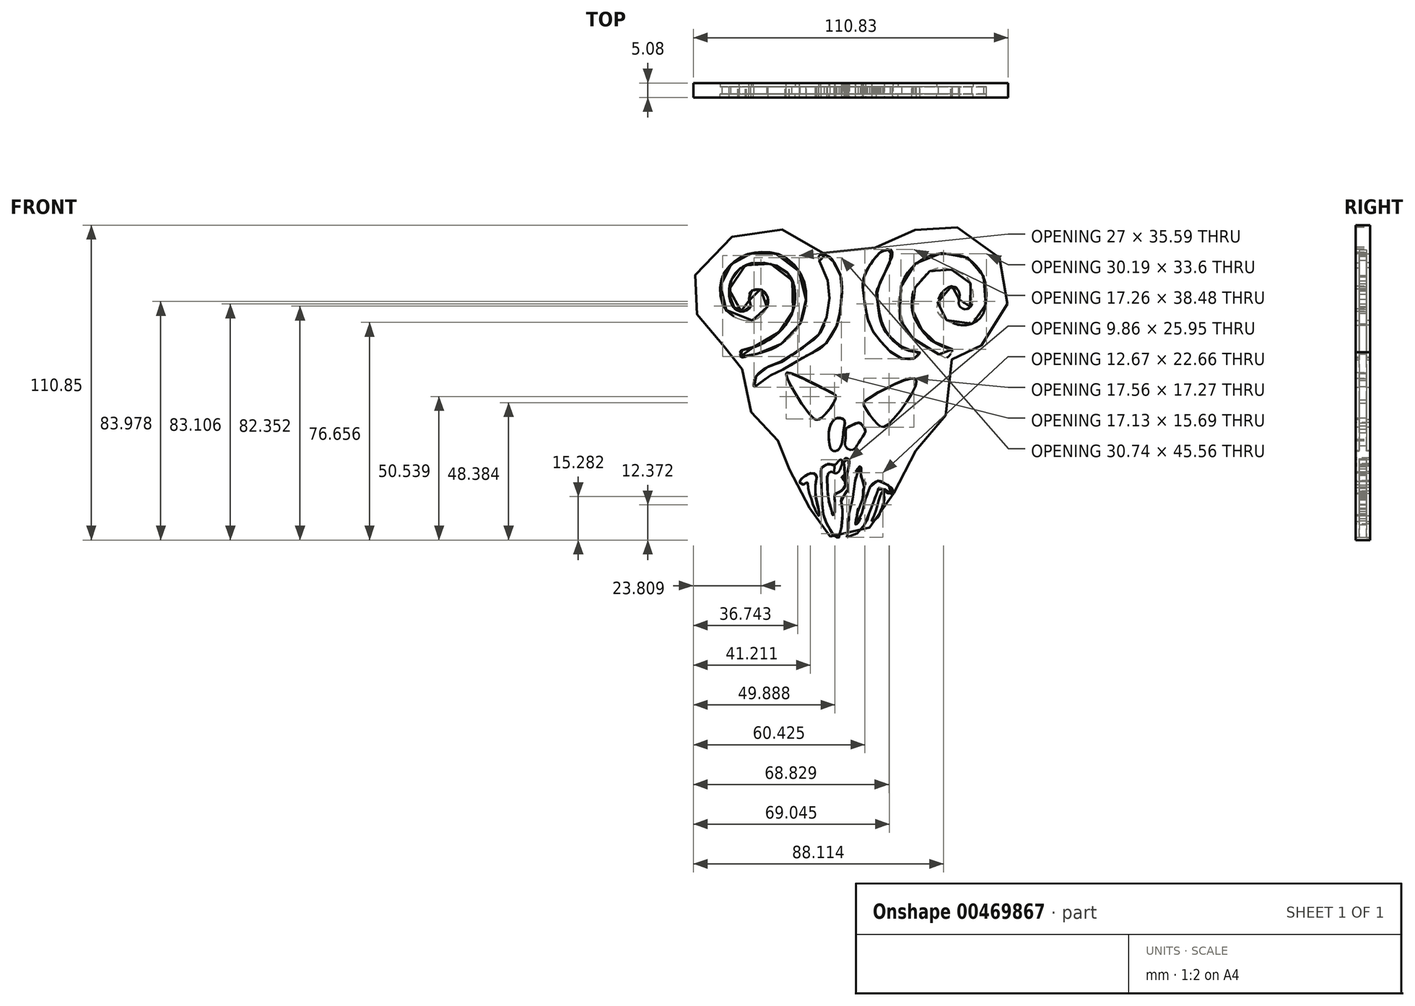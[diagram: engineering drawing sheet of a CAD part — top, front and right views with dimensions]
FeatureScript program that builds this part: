
annotation { "Feature Type Name" : "Feature", "Feature Type Description" : "" }
export const myFeature = defineFeature(function(context is Context, id is Id, definition is map)
    precondition{}
    {
        {
            var Q0;
            Q0=qCreatedBy(makeId("Front.planeOp"),FACE);
            var sketch = newSketch(context, id + "F0", { "sketchPlane" : qUnion([Q0])});
            skFitSpline(sketch, "E0", {"points": [v(-12.41, -53.78) * mm, v(-13.63, -52.56) * mm, v(-14.64, -51.27) * mm, v(-16.07, -48.61) * mm, v(-17.07, -46.75) * mm, v(-18.08, -45.96) * mm, v(-19.44, -44.02) * mm, v(-21.02, -40.22) * mm, v(-21.73, -36.85) * mm, v(-23.67, -34.85) * mm, v(-25.53, -33.48) * mm, v(-26.83, -29.18) * mm, v(-26.97, -24.38) * mm, v(-28.16, -22.07) * mm, v(-28.2, -20.86) * mm, v(-28.66, -19.84) * mm, v(-29.83, -19.49) * mm, v(-30.6, -19.95) * mm, v(-32.21, -19.34) * mm, v(-33.53, -18.22) * mm, v(-35.07, -16.98) * mm, v(-37.5, -14.85) * mm, v(-39.28, -11.7) * mm, v(-40.8, -8.46) * mm, v(-41.82, -4.66) * mm, v(-42.17, 0.56) * mm, v(-41.92, 4.31) * mm, v(-42.41, 4.65) * mm, v(-43.99, 5.58) * mm, v(-44.7, 6.84) * mm, v(-44.92, 9.53) * mm, v(-44.78, 10.57) * mm, v(-45.6, 11.5) * mm, v(-47.18, 12.29) * mm, v(-49.55, 12.97) * mm, v(-52.34, 14.87) * mm, v(-54.7, 16.88) * mm, v(-56.61, 19.1) * mm, v(-58.12, 21.33) * mm, v(-59.23, 24.41) * mm, v(-59.59, 28) * mm, v(-60.27, 29.9) * mm, v(-60.55, 31.3) * mm, v(-60.48, 34.74) * mm, v(-60.23, 36.32) * mm, v(-58.58, 42.24) * mm, v(-54.9, 47) * mm, v(-53.57, 48.12) * mm, v(-47.83, 51) * mm, v(-46.38, 52.27) * mm, v(-43.1, 53.98) * mm, v(-39.33, 54.83) * mm, v(-32.87, 55.1) * mm, v(-27.93, 53.68) * mm, v(-23.02, 51) * mm, v(-19.58, 48.32) * mm, v(-18.07, 46.8) * mm, v(-15.48, 46.04) * mm, v(-13.38, 46.01) * mm, v(-8.59, 47.13) * mm, v(-3.47, 47.86) * mm, v(1.55, 48.2) * mm, v(6.35, 47.57) * mm, v(8.34, 47.96) * mm, v(11.9, 50.37) * mm, v(13.92, 51.76) * mm, v(16.96, 53.9) * mm, v(21.24, 55.38) * mm, v(23.47, 55.7) * mm, v(26.85, 55.74) * mm, v(29.01, 55.2) * mm, v(32.13, 55.02) * mm, v(37.5, 53.44) * mm, v(42.35, 50.4) * mm, v(45.15, 47.53) * mm, v(47.07, 44.5) * mm, v(48.4, 40.87) * mm, v(49.26, 37.18) * mm, v(50.13, 33.8) * mm, v(50.13, 29.7) * mm, v(49.6, 26.44) * mm, v(48.76, 23.71) * mm, v(46.41, 18.89) * mm, v(43.47, 15.64) * mm, v(39.93, 12.92) * mm, v(37.8, 11.95) * mm, v(34.7, 11.1) * mm, v(31.72, 10.98) * mm, v(30.08, 9.78) * mm, v(30, 9.52) * mm, v(30.44, 8.63) * mm, v(30.11, 6.75) * mm, v(29.07, -2.21) * mm, v(28.98, -4.8) * mm, v(28.46, -10.58) * mm, v(26.92, -13.88) * mm, v(25.3, -16.42) * mm, v(21.24, -20.64) * mm, v(18.57, -22.74) * mm, v(17.4, -23.93) * mm, v(14.42, -28.1) * mm, v(13.02, -31.72) * mm, v(12.4, -34) * mm, v(10.28, -37.84) * mm, v(8.99, -40.56) * mm, v(7.4, -44.15) * mm, v(6.26, -46.8) * mm, v(3.97, -48.52) * mm, v(1.82, -50.31) * mm, v(-1.41, -52.54) * mm, v(-3.5, -54.04) * mm, v(-6.02, -54.93) * mm, v(-9.06, -54.87) * mm, v(-12.41, -53.78) * mm]});
            skFitSpline(sketch, "E1", {"points": [v(-44.06, 9.53) * mm, v(-41.4, 9.75) * mm, v(-39.23, 10.21) * mm, v(-35.27, 11.4) * mm, v(-30.44, 13.55) * mm, v(-24.14, 19.03) * mm, v(-22.67, 21.83) * mm, v(-21.44, 26.26) * mm, v(-20.94, 33.49) * mm, v(-23.8, 40.3) * mm, v(-29.5, 45.2) * mm, v(-35.56, 46.4) * mm, v(-39.7, 46.04) * mm, v(-43.83, 44.6) * mm, v(-47.28, 41.99) * mm, v(-50, 38.5) * mm, v(-51.13, 33.16) * mm, v(-50.2, 27.98) * mm, v(-46.32, 23.64) * mm, v(-39.53, 22.4) * mm, v(-36.48, 24.33) * mm, v(-34.63, 26.86) * mm, v(-34.4, 30.75) * mm, v(-36.64, 33.2) * mm, v(-40.05, 32.8) * mm, v(-41.1, 30.35) * mm, v(-40.25, 27.9) * mm, v(-41.02, 26.45) * mm, v(-44.39, 25.73) * mm, v(-47.48, 29.34) * mm, v(-46.96, 37.01) * mm, v(-42.02, 41.79) * mm, v(-36.84, 42.63) * mm, v(-31.14, 41.5) * mm, v(-26.2, 37.45) * mm, v(-24.76, 29.67) * mm, v(-26.48, 23.28) * mm, v(-29.86, 18.75) * mm, v(-34.08, 15.52) * mm, v(-40.95, 12.47) * mm, v(-43.96, 11.5) * mm, v(-44.06, 9.53) * mm]});
            skFitSpline(sketch, "E2", {"points": [v(30.65, 12.15) * mm, v(28.89, 12.79) * mm, v(25.07, 14.35) * mm, v(22.95, 15.68) * mm, v(20.54, 18.25) * mm, v(18.81, 20.62) * mm, v(16.93, 24.4) * mm, v(16.36, 29.13) * mm, v(17.2, 33.2) * mm, v(19.57, 36.71) * mm, v(22.72, 39.67) * mm, v(26.5, 40.87) * mm, v(31.03, 39.91) * mm, v(35.53, 37.59) * mm, v(37.73, 32.69) * mm, v(37.37, 27.8) * mm, v(35.32, 26.43) * mm, v(33.08, 27.75) * mm, v(33.24, 31.12) * mm, v(32.2, 33.81) * mm, v(30.08, 34.41) * mm, v(27.26, 32.57) * mm, v(25.17, 27.43) * mm, v(25.93, 24.38) * mm, v(30.79, 21.33) * mm, v(36.69, 20.85) * mm, v(40.9, 23.82) * mm, v(42.47, 28.63) * mm, v(42.15, 36.18) * mm, v(39.78, 40.87) * mm, v(35.79, 44.47) * mm, v(30.08, 45.84) * mm, v(23.54, 45.56) * mm, v(17.36, 42.06) * mm, v(13.79, 37.37) * mm, v(11.58, 29.3) * mm, v(12.74, 20.67) * mm, v(15.2, 17.41) * mm, v(20.2, 13.4) * mm, v(26.95, 9.78) * mm, v(28.78, 9.24) * mm, v(30.65, 12.15) * mm]});
            skFitSpline(sketch, "E3", {"points": [v(17.1, 8.84) * mm, v(19.19, 10.98) * mm, v(15.78, 11.74) * mm, v(11.73, 13.8) * mm, v(8.05, 17.28) * mm, v(5.18, 23.15) * mm, v(4.13, 30.54) * mm, v(4.23, 33.58) * mm, v(9.46, 46.68) * mm, v(6.35, 46.98) * mm, v(4.04, 45.09) * mm, v(2.34, 43) * mm, v(-0.56, 37.42) * mm, v(-0.68, 31.15) * mm, v(1.49, 20.75) * mm, v(4.92, 15.43) * mm, v(10.84, 9.78) * mm, v(17.1, 8.84) * mm]});
            skFitSpline(sketch, "E4", {"points": [v(-39.2, -1.16) * mm, v(-39.07, 1.55) * mm, v(-34.88, 5.76) * mm, v(-29.65, 7.8) * mm, v(-26.48, 9.78) * mm, v(-20.68, 13.83) * mm, v(-15.18, 19.2) * mm, v(-12.81, 28.76) * mm, v(-13.48, 36.88) * mm, v(-16.3, 45.12) * mm, v(-12.57, 44.93) * mm, v(-10.47, 41.68) * mm, v(-8.47, 37.3) * mm, v(-8.66, 27.65) * mm, v(-9.9, 20.97) * mm, v(-14.96, 13.23) * mm, v(-21.44, 9.53) * mm, v(-27.76, 5.6) * mm, v(-32.53, 3.4) * mm, v(-35.46, 1.55) * mm, v(-36.37, 0.73) * mm, v(-39.2, -1.16) * mm]});
            skFitSpline(sketch, "E5", {"points": [v(-27.93, 3.35) * mm, v(-19.39, -11.02) * mm, v(-15.9, -12.26) * mm, v(-10.41, -4.86) * mm, v(-12.6, -2.66) * mm, v(-26.98, 3.97) * mm, v(-27.93, 3.35) * mm]});
            skFitSpline(sketch, "E6", {"points": [v(-0.53, -7.63) * mm, v(4.3, -14.26) * mm, v(7.35, -14.79) * mm, v(18, 0.63) * mm, v(15.56, 1.87) * mm, v(0, -5.96) * mm, v(-0.53, -7.63) * mm]});
            skFitSpline(sketch, "E7", {"points": [v(-8.85, -11.98) * mm, v(-10.8, -12.41) * mm, v(-12.52, -15.18) * mm, v(-12.86, -19.67) * mm, v(-11.76, -23.44) * mm, v(-9.7, -23.34) * mm, v(-8.23, -20.64) * mm, v(-7.56, -15.85) * mm, v(-7.37, -12.8) * mm, v(-8.85, -11.98) * mm]});
            skFitSpline(sketch, "E8", {"points": [v(-7.13, -21.72) * mm, v(-6.9, -18.57) * mm, v(-6.84, -15.85) * mm, v(-5.32, -14.8) * mm, v(-2.36, -13.65) * mm, v(-1.26, -14.26) * mm, v(0, -16.28) * mm, v(-0.64, -18.14) * mm, v(-2.3, -20.64) * mm, v(-3.26, -22.2) * mm, v(-5.08, -23.4) * mm, v(-7.13, -21.72) * mm]});
            skFitSpline(sketch, "E9", {"points": [v(-16.42, -46.46) * mm, v(-16.28, -45.17) * mm, v(-16.42, -44.15) * mm, v(-16.76, -42.76) * mm, v(-17.07, -41.52) * mm, v(-17.4, -39.94) * mm, v(-17.55, -38.13) * mm, v(-17.57, -36.58) * mm, v(-17.48, -34.9) * mm, v(-17.07, -33.07) * mm, v(-17.33, -32.07) * mm, v(-18.08, -31.4) * mm, v(-19.58, -31.5) * mm, v(-21.58, -32.6) * mm, v(-22.75, -33.69) * mm, v(-23.23, -34.55) * mm, v(-22.58, -35.03) * mm, v(-21.63, -35.53) * mm, v(-20.91, -35.05) * mm, v(-20.53, -34.38) * mm, v(-20.3, -35.2) * mm, v(-20.12, -37.06) * mm, v(-19.7, -38.54) * mm, v(-18.9, -40.9) * mm, v(-18.45, -42.57) * mm, v(-17.69, -44.15) * mm, v(-17.55, -44.65) * mm, v(-17.07, -45.6) * mm, v(-16.42, -46.46) * mm]});
            skFitSpline(sketch, "E10", {"points": [v(-6.5, -53.99) * mm, v(-6.41, -53.06) * mm, v(-6.05, -51.66) * mm, v(-5.93, -49.33) * mm, v(-5.97, -46.68) * mm, v(-5.13, -43.3) * mm, v(-4.44, -40.02) * mm, v(-3.6, -34.92) * mm, v(-3.36, -31.03) * mm, v(-1.77, -28.98) * mm, v(-1.36, -30.33) * mm, v(-1.36, -32.9) * mm, v(0, -34.85) * mm, v(-0.69, -36.95) * mm, v(-0.76, -39.44) * mm, v(-1.63, -42.01) * mm, v(-2.58, -44.17) * mm, v(-3.12, -47.14) * mm, v(-3.4, -49.37) * mm, v(-2.3, -48.42) * mm, v(-1.36, -46.13) * mm, v(-0.69, -43.7) * mm, v(0, -40.73) * mm, v(0.93, -38.43) * mm, v(1.8, -36) * mm, v(2.69, -34.99) * mm, v(4.3, -34.11) * mm, v(6.47, -34.52) * mm, v(8.02, -35.66) * mm, v(9.57, -36.88) * mm, v(9.28, -38.57) * mm, v(8.68, -38.58) * mm, v(7.36, -38.28) * mm, v(7.03, -37.22) * mm, v(6.03, -36.9) * mm, v(4.75, -36.5) * mm, v(4.47, -37.3) * mm, v(3.7, -39.11) * mm, v(2.9, -41.44) * mm, v(2.14, -43.45) * mm, v(1.18, -46.06) * mm, v(0.5, -48.39) * mm, v(-0.71, -50.15) * mm, v(-1.87, -51.84) * mm, v(-3.08, -52.72) * mm, v(-4.12, -53.44) * mm, v(-6.5, -53.99) * mm]});
            skFitSpline(sketch, "E11", {"points": [v(2.22, -48.47) * mm, v(2.74, -47.06) * mm, v(3.79, -44.17) * mm, v(6.03, -37.84) * mm, v(6.36, -37.84) * mm, v(6.52, -39) * mm, v(6.68, -40.6) * mm, v(6.32, -42.2) * mm, v(5.51, -44.3) * mm, v(4.83, -46.18) * mm, v(3.83, -47.58) * mm, v(2.22, -48.47) * mm]});
            skFitSpline(sketch, "E12", {"points": [v(-10.84, -28.5) * mm, v(-12.66, -28.16) * mm, v(-15.27, -29.4) * mm, v(-15.61, -32.81) * mm, v(-15.27, -40.99) * mm, v(-14.82, -45.53) * mm, v(-13.9, -48.7) * mm, v(-12.43, -51.32) * mm, v(-11.56, -53) * mm, v(-10.48, -53.77) * mm, v(-9.4, -54.13) * mm, v(-9.07, -53.25) * mm, v(-8.6, -51.44) * mm, v(-8.27, -48.95) * mm, v(-8.03, -45.5) * mm, v(-8.15, -43.41) * mm, v(-8.27, -39.84) * mm, v(-6.8, -38.75) * mm, v(-6.23, -36.36) * mm, v(-6.68, -33.07) * mm, v(-6, -30) * mm, v(-5.78, -28.64) * mm, v(-6, -26.48) * mm, v(-7.37, -26.48) * mm, v(-7.37, -31.72) * mm, v(-8.3, -32.9) * mm, v(-7.37, -34.21) * mm, v(-7.37, -36.5) * mm, v(-9.06, -37.97) * mm, v(-10.08, -38.48) * mm, v(-10.57, -38.5) * mm, v(-10.82, -39.94) * mm, v(-10.76, -42.26) * mm, v(-10.74, -43.9) * mm, v(-10.85, -45.63) * mm, v(-11.36, -46.06) * mm, v(-11.84, -44.56) * mm, v(-12.5, -42.57) * mm, v(-12.95, -40.33) * mm, v(-13.23, -37.71) * mm, v(-13.43, -34.28) * mm, v(-13.35, -32.24) * mm, v(-12.33, -30.96) * mm, v(-10.88, -31.47) * mm, v(-9.66, -31.21) * mm, v(-8.35, -28.57) * mm, v(-8.32, -26.87) * mm, v(-9.03, -26.87) * mm, v(-9.83, -27.6) * mm, v(-10.84, -28.5) * mm]});
            skLineSegment(sketch, "E13", {"start": v(-7.37, -34.21) * mm, "end": v(-7.37, -31.72) * mm});
            skFitSpline(sketch, "E14", {"points": [v(-10.84, -28.5) * mm, v(-10.88, -31.47) * mm], "startDerivative": vector(-0.03, -2.97) * mm, "endDerivative": vector(-0.03, -2.97) * mm});
            skSolve(sketch);
        }
        {
            var Q0;
            Q0 = qSketchRegion(id + "F0", true);
            extrude(context, id + "F1", {"entities" : qUnion([Q0]), "endBound" : BoundingType.SYMMETRIC, "depth" : 5.08 * mm});
        }
        {
            var Q0;
            Q0=qCreatedBy(makeId("Front.planeOp"),FACE);
            var sketch = newSketch(context, id + "F2", { "sketchPlane" : qUnion([Q0])});
            skFitSpline(sketch, "E15", {"points": [v(-12.48, -53.96) * mm, v(-13.7, -52.75) * mm, v(-14.7, -51.45) * mm, v(-16.14, -48.8) * mm, v(-17.14, -46.94) * mm, v(-18.15, -46.15) * mm, v(-19.51, -44.21) * mm, v(-21.09, -40.41) * mm, v(-21.8, -37.04) * mm, v(-23.74, -35.03) * mm, v(-25.6, -33.67) * mm, v(-26.9, -29.37) * mm, v(-27.04, -24.57) * mm, v(-28.23, -22.26) * mm, v(-28.28, -21.05) * mm, v(-28.74, -20.03) * mm, v(-29.9, -19.68) * mm, v(-30.66, -20.13) * mm, v(-32.28, -19.53) * mm, v(-33.6, -18.41) * mm, v(-35.15, -17.17) * mm, v(-37.58, -15.04) * mm, v(-39.35, -11.9) * mm, v(-40.88, -8.65) * mm, v(-41.89, -4.85) * mm, v(-42.24, 0.37) * mm, v(-42, 4.13) * mm, v(-42.48, 4.46) * mm, v(-44.06, 5.4) * mm, v(-44.78, 6.65) * mm, v(-45, 9.34) * mm, v(-44.85, 10.38) * mm, v(-45.67, 11.31) * mm, v(-47.25, 12.1) * mm, v(-49.62, 12.78) * mm, v(-52.41, 14.68) * mm, v(-54.78, 16.69) * mm, v(-56.68, 18.92) * mm, v(-58.19, 21.14) * mm, v(-59.3, 24.22) * mm, v(-59.66, 27.81) * mm, v(-60.34, 29.71) * mm, v(-60.63, 31.1) * mm, v(-60.55, 34.55) * mm, v(-60.3, 36.13) * mm, v(-58.65, 42.05) * mm, v(-54.97, 46.81) * mm, v(-53.65, 47.93) * mm, v(-47.9, 50.81) * mm, v(-46.45, 52.08) * mm, v(-43.17, 53.8) * mm, v(-39.4, 54.64) * mm, v(-32.95, 54.91) * mm, v(-28, 53.5) * mm, v(-23.09, 50.81) * mm, v(-19.65, 48.13) * mm, v(-18.14, 46.6) * mm, v(-15.55, 45.85) * mm, v(-13.45, 45.82) * mm, v(-8.66, 46.94) * mm, v(-3.54, 47.67) * mm, v(1.48, 48) * mm, v(6.28, 47.38) * mm, v(8.27, 47.77) * mm, v(11.82, 50.18) * mm, v(13.84, 51.57) * mm, v(16.89, 53.7) * mm, v(21.17, 55.19) * mm, v(23.4, 55.52) * mm, v(26.78, 55.55) * mm, v(28.94, 55.01) * mm, v(32.06, 54.83) * mm, v(37.44, 53.26) * mm, v(42.28, 50.2) * mm, v(45.07, 47.34) * mm, v(47, 44.3) * mm, v(48.33, 40.68) * mm, v(49.2, 37) * mm, v(50.05, 33.6) * mm, v(50.05, 29.51) * mm, v(49.52, 26.25) * mm, v(48.7, 23.53) * mm, v(46.34, 18.7) * mm, v(43.4, 15.46) * mm, v(39.86, 12.73) * mm, v(37.73, 11.76) * mm, v(34.63, 10.9) * mm, v(31.65, 10.8) * mm, v(30, 9.59) * mm, v(29.92, 9.33) * mm, v(30.37, 8.44) * mm, v(30.04, 6.56) * mm, v(29, -2.4) * mm, v(28.9, -4.98) * mm, v(28.39, -10.77) * mm, v(26.84, -14.06) * mm, v(25.23, -16.61) * mm, v(21.17, -20.83) * mm, v(18.5, -22.93) * mm, v(17.34, -24.12) * mm, v(14.35, -28.3) * mm, v(12.95, -31.91) * mm, v(12.32, -34.2) * mm, v(10.2, -38.03) * mm, v(8.91, -40.75) * mm, v(7.34, -44.34) * mm, v(6.2, -46.99) * mm, v(3.9, -48.71) * mm, v(1.74, -50.5) * mm, v(-1.48, -52.73) * mm, v(-3.56, -54.23) * mm, v(-6.1, -55.11) * mm, v(-9.13, -55.06) * mm, v(-12.48, -53.96) * mm]});
            skFitSpline(sketch, "E16", {"points": [v(-44.14, 9.34) * mm, v(-41.47, 9.56) * mm, v(-39.3, 10.03) * mm, v(-35.35, 11.2) * mm, v(-30.5, 13.36) * mm, v(-24.21, 18.84) * mm, v(-22.74, 21.64) * mm, v(-21.5, 26.07) * mm, v(-21, 33.3) * mm, v(-23.87, 40.12) * mm, v(-29.57, 45.01) * mm, v(-35.63, 46.22) * mm, v(-39.76, 45.86) * mm, v(-43.9, 44.41) * mm, v(-47.35, 41.8) * mm, v(-50.08, 38.3) * mm, v(-51.2, 32.97) * mm, v(-50.28, 27.8) * mm, v(-46.39, 23.46) * mm, v(-39.6, 22.21) * mm, v(-36.55, 24.14) * mm, v(-34.7, 26.67) * mm, v(-34.46, 30.56) * mm, v(-36.71, 33) * mm, v(-40.12, 32.6) * mm, v(-41.17, 30.16) * mm, v(-40.32, 27.71) * mm, v(-41.09, 26.27) * mm, v(-44.46, 25.54) * mm, v(-47.55, 29.16) * mm, v(-47.03, 36.82) * mm, v(-42.1, 41.6) * mm, v(-36.91, 42.44) * mm, v(-31.21, 41.32) * mm, v(-26.27, 37.26) * mm, v(-24.83, 29.48) * mm, v(-26.56, 23.1) * mm, v(-29.93, 18.56) * mm, v(-34.15, 15.33) * mm, v(-41.02, 12.28) * mm, v(-44.03, 11.32) * mm, v(-44.14, 9.34) * mm]});
            skFitSpline(sketch, "E17", {"points": [v(30.58, 11.96) * mm, v(28.82, 12.6) * mm, v(25, 14.17) * mm, v(22.88, 15.5) * mm, v(20.47, 18.06) * mm, v(18.74, 20.43) * mm, v(16.85, 24.2) * mm, v(16.3, 28.94) * mm, v(17.13, 33) * mm, v(19.5, 36.53) * mm, v(22.65, 39.48) * mm, v(26.42, 40.68) * mm, v(30.96, 39.73) * mm, v(35.45, 37.4) * mm, v(37.66, 32.5) * mm, v(37.3, 27.6) * mm, v(35.25, 26.24) * mm, v(33, 27.56) * mm, v(33.17, 30.93) * mm, v(32.12, 33.62) * mm, v(30, 34.23) * mm, v(27.18, 32.38) * mm, v(25.1, 27.24) * mm, v(25.86, 24.19) * mm, v(30.72, 21.14) * mm, v(36.62, 20.66) * mm, v(40.83, 23.63) * mm, v(42.4, 28.44) * mm, v(42.08, 36) * mm, v(39.7, 40.68) * mm, v(35.71, 44.28) * mm, v(30, 45.65) * mm, v(23.47, 45.37) * mm, v(17.29, 41.87) * mm, v(13.72, 37.18) * mm, v(11.5, 29.1) * mm, v(12.67, 20.48) * mm, v(15.13, 17.22) * mm, v(20.13, 13.2) * mm, v(26.88, 9.59) * mm, v(28.7, 9.05) * mm, v(30.58, 11.96) * mm]});
            skFitSpline(sketch, "E18", {"points": [v(17.02, 8.65) * mm, v(19.12, 10.8) * mm, v(15.7, 11.55) * mm, v(11.66, 13.61) * mm, v(7.98, 17.09) * mm, v(5.1, 22.96) * mm, v(4.06, 30.35) * mm, v(4.16, 33.4) * mm, v(9.39, 46.5) * mm, v(6.28, 46.8) * mm, v(3.97, 44.9) * mm, v(2.27, 42.8) * mm, v(-0.63, 37.23) * mm, v(-0.75, 30.97) * mm, v(1.42, 20.57) * mm, v(4.85, 15.24) * mm, v(10.77, 9.59) * mm, v(17.02, 8.65) * mm]});
            skFitSpline(sketch, "E19", {"points": [v(-39.28, -1.34) * mm, v(-39.14, 1.36) * mm, v(-34.96, 5.58) * mm, v(-29.72, 7.6) * mm, v(-26.55, 9.59) * mm, v(-20.75, 13.64) * mm, v(-15.25, 19) * mm, v(-12.89, 28.57) * mm, v(-13.55, 36.69) * mm, v(-16.37, 44.93) * mm, v(-12.65, 44.74) * mm, v(-10.55, 41.5) * mm, v(-8.54, 37.1) * mm, v(-8.73, 27.46) * mm, v(-9.97, 20.78) * mm, v(-15.03, 13.04) * mm, v(-21.5, 9.34) * mm, v(-27.83, 5.4) * mm, v(-32.6, 3.2) * mm, v(-35.53, 1.36) * mm, v(-36.44, 0.54) * mm, v(-39.28, -1.34) * mm]});
            skFitSpline(sketch, "E20", {"points": [v(-28, 3.16) * mm, v(-19.46, -11.2) * mm, v(-15.97, -12.45) * mm, v(-10.48, -5.05) * mm, v(-12.68, -2.85) * mm, v(-27.05, 3.78) * mm, v(-28, 3.16) * mm]});
            skFitSpline(sketch, "E21", {"points": [v(-0.6, -7.82) * mm, v(4.22, -14.45) * mm, v(7.27, -14.98) * mm, v(17.92, 0.44) * mm, v(15.49, 1.68) * mm, v(-0.07, -6.14) * mm, v(-0.6, -7.82) * mm]});
            skFitSpline(sketch, "E22", {"points": [v(-8.92, -12.17) * mm, v(-10.88, -12.6) * mm, v(-12.6, -15.37) * mm, v(-12.93, -19.86) * mm, v(-11.83, -23.63) * mm, v(-9.78, -23.53) * mm, v(-8.3, -20.83) * mm, v(-7.63, -16.04) * mm, v(-7.44, -12.98) * mm, v(-8.92, -12.17) * mm]});
            skFitSpline(sketch, "E23", {"points": [v(-7.2, -21.91) * mm, v(-6.96, -18.76) * mm, v(-6.92, -16.04) * mm, v(-5.39, -14.99) * mm, v(-2.43, -13.84) * mm, v(-1.33, -14.45) * mm, v(-0.07, -16.47) * mm, v(-0.7, -18.33) * mm, v(-2.38, -20.83) * mm, v(-3.33, -22.39) * mm, v(-5.15, -23.58) * mm, v(-7.2, -21.91) * mm]});
            skFitSpline(sketch, "E24", {"points": [v(-16.5, -46.65) * mm, v(-16.35, -45.36) * mm, v(-16.5, -44.34) * mm, v(-16.83, -42.95) * mm, v(-17.14, -41.7) * mm, v(-17.47, -40.13) * mm, v(-17.62, -38.32) * mm, v(-17.64, -36.77) * mm, v(-17.55, -35.1) * mm, v(-17.14, -33.26) * mm, v(-17.4, -32.26) * mm, v(-18.15, -31.59) * mm, v(-19.65, -31.68) * mm, v(-21.65, -32.78) * mm, v(-22.82, -33.88) * mm, v(-23.3, -34.74) * mm, v(-22.65, -35.22) * mm, v(-21.7, -35.72) * mm, v(-20.98, -35.24) * mm, v(-20.6, -34.57) * mm, v(-20.36, -35.38) * mm, v(-20.2, -37.24) * mm, v(-19.77, -38.72) * mm, v(-18.98, -41.09) * mm, v(-18.53, -42.76) * mm, v(-17.76, -44.34) * mm, v(-17.62, -44.83) * mm, v(-17.14, -45.79) * mm, v(-16.5, -46.65) * mm]});
            skFitSpline(sketch, "E25", {"points": [v(-6.56, -54.18) * mm, v(-6.48, -53.25) * mm, v(-6.12, -51.85) * mm, v(-6, -49.52) * mm, v(-6.04, -46.87) * mm, v(-5.2, -43.5) * mm, v(-4.52, -40.2) * mm, v(-3.67, -35.1) * mm, v(-3.43, -31.21) * mm, v(-1.84, -29.17) * mm, v(-1.44, -30.52) * mm, v(-1.44, -33.08) * mm, v(-0.07, -35.04) * mm, v(-0.76, -37.14) * mm, v(-0.83, -39.63) * mm, v(-1.7, -42.2) * mm, v(-2.65, -44.36) * mm, v(-3.2, -47.33) * mm, v(-3.46, -49.56) * mm, v(-2.38, -48.61) * mm, v(-1.44, -46.32) * mm, v(-0.76, -43.89) * mm, v(-0.07, -40.92) * mm, v(0.86, -38.62) * mm, v(1.74, -36.2) * mm, v(2.61, -35.18) * mm, v(4.23, -34.3) * mm, v(6.4, -34.7) * mm, v(7.95, -35.85) * mm, v(9.5, -37.07) * mm, v(9.2, -38.76) * mm, v(8.6, -38.77) * mm, v(7.29, -38.47) * mm, v(6.96, -37.4) * mm, v(5.96, -37.1) * mm, v(4.68, -36.7) * mm, v(4.4, -37.5) * mm, v(3.63, -39.3) * mm, v(2.83, -41.63) * mm, v(2.07, -43.64) * mm, v(1.1, -46.25) * mm, v(0.42, -48.57) * mm, v(-0.78, -50.34) * mm, v(-1.95, -52.03) * mm, v(-3.15, -52.9) * mm, v(-4.2, -53.63) * mm, v(-6.56, -54.18) * mm]});
            skFitSpline(sketch, "E26", {"points": [v(2.15, -48.65) * mm, v(2.67, -47.25) * mm, v(3.71, -44.36) * mm, v(5.96, -38.03) * mm, v(6.28, -38.03) * mm, v(6.44, -39.18) * mm, v(6.6, -40.79) * mm, v(6.24, -42.4) * mm, v(5.44, -44.48) * mm, v(4.76, -46.37) * mm, v(3.75, -47.77) * mm, v(2.15, -48.65) * mm]});
            skFitSpline(sketch, "E27", {"points": [v(-10.92, -28.69) * mm, v(-12.73, -28.35) * mm, v(-15.34, -29.6) * mm, v(-15.68, -33) * mm, v(-15.34, -41.18) * mm, v(-14.89, -45.72) * mm, v(-13.98, -48.9) * mm, v(-12.5, -51.51) * mm, v(-11.63, -53.2) * mm, v(-10.55, -53.96) * mm, v(-9.47, -54.32) * mm, v(-9.14, -53.44) * mm, v(-8.66, -51.63) * mm, v(-8.34, -49.14) * mm, v(-8.1, -45.69) * mm, v(-8.22, -43.6) * mm, v(-8.34, -40.03) * mm, v(-6.87, -38.94) * mm, v(-6.3, -36.55) * mm, v(-6.76, -33.26) * mm, v(-6.08, -30.2) * mm, v(-5.85, -28.83) * mm, v(-6.07, -26.67) * mm, v(-7.44, -26.67) * mm, v(-7.44, -31.91) * mm, v(-8.37, -33.08) * mm, v(-7.44, -34.4) * mm, v(-7.44, -36.7) * mm, v(-9.13, -38.16) * mm, v(-10.15, -38.67) * mm, v(-10.64, -38.7) * mm, v(-10.9, -40.13) * mm, v(-10.84, -42.45) * mm, v(-10.8, -44.1) * mm, v(-10.92, -45.82) * mm, v(-11.43, -46.25) * mm, v(-11.91, -44.74) * mm, v(-12.57, -42.76) * mm, v(-13.02, -40.51) * mm, v(-13.3, -37.9) * mm, v(-13.5, -34.47) * mm, v(-13.42, -32.42) * mm, v(-12.4, -31.15) * mm, v(-10.95, -31.66) * mm, v(-9.73, -31.4) * mm, v(-8.42, -28.76) * mm, v(-8.4, -27.06) * mm, v(-9.1, -27.06) * mm, v(-9.9, -27.8) * mm, v(-10.92, -28.69) * mm]});
            skLineSegment(sketch, "E28", {"start": v(-7.44, -34.4) * mm, "end": v(-7.44, -31.91) * mm});
            skFitSpline(sketch, "E29", {"points": [v(-10.92, -28.69) * mm, v(-10.95, -31.66) * mm], "startDerivative": vector(-0.03, -2.97) * mm, "endDerivative": vector(-0.03, -2.97) * mm});
            skSolve(sketch);
        }
        {
            var Q0;
            Q0=makeQuery(id+"F2.imprint","IMPRINT",FACE,{"disambiguationData":[TD([[makeQuery(id+"F2.imprint","IMPRINT",EDGE,{"derivedFrom":sQuery(id+"F2.wireOp",EDGE,"E16")}),1.0]])]});
            var Q1;
            Q1=makeQuery(id+"F2.imprint","IMPRINT",FACE,{"disambiguationData":[TD([[makeQuery(id+"F2.imprint","IMPRINT",EDGE,{"derivedFrom":sQuery(id+"F2.wireOp",EDGE,"E18")}),1.0]])]});
            var Q2;
            Q2=makeQuery(id+"F2.imprint","IMPRINT",FACE,{"disambiguationData":[TD([[makeQuery(id+"F2.imprint","IMPRINT",EDGE,{"derivedFrom":sQuery(id+"F2.wireOp",EDGE,"E17")}),1.0]])]});
            var Q3;
            Q3=makeQuery(id+"F2.imprint","IMPRINT",FACE,{"disambiguationData":[TD([[makeQuery(id+"F2.imprint","IMPRINT",EDGE,{"derivedFrom":sQuery(id+"F2.wireOp",EDGE,"E21")}),1.0]])]});
            var Q4;
            Q4=makeQuery(id+"F2.imprint","IMPRINT",FACE,{"disambiguationData":[TD([[makeQuery(id+"F2.imprint","IMPRINT",EDGE,{"derivedFrom":sQuery(id+"F2.wireOp",EDGE,"E20")}),1.0]])]});
            var Q5;
            Q5=makeQuery(id+"F2.imprint","IMPRINT",FACE,{"disambiguationData":[TD([[makeQuery(id+"F2.imprint","IMPRINT",EDGE,{"derivedFrom":sQuery(id+"F2.wireOp",EDGE,"E22")}),1.0]])]});
            var Q6;
            Q6=makeQuery(id+"F2.imprint","IMPRINT",FACE,{"disambiguationData":[TD([[makeQuery(id+"F2.imprint","IMPRINT",EDGE,{"derivedFrom":sQuery(id+"F2.wireOp",EDGE,"E23")}),-1.0]])]});
            var Q7;
            Q7=makeQuery(id+"F2.imprint","IMPRINT",FACE,{"disambiguationData":[TD([[makeQuery(id+"F2.imprint","IMPRINT",EDGE,{"derivedFrom":sQuery(id+"F2.wireOp",EDGE,"E27")}),1.0]])]});
            var Q8;
            Q8=makeQuery(id+"F2.imprint","IMPRINT",FACE,{"disambiguationData":[TD([[makeQuery(id+"F2.imprint","IMPRINT",EDGE,{"derivedFrom":sQuery(id+"F2.wireOp",EDGE,"E24")}),1.0]])]});
            var Q9;
            Q9=makeQuery(id+"F2.imprint","IMPRINT",FACE,{"disambiguationData":[TD([[makeQuery(id+"F2.imprint","IMPRINT",EDGE,{"derivedFrom":sQuery(id+"F2.wireOp",EDGE,"E26")}),-1.0]])]});
            var Q10;
            Q10=makeQuery(id+"F2.imprint","IMPRINT",FACE,{"disambiguationData":[TD([[makeQuery(id+"F2.imprint","IMPRINT",EDGE,{"derivedFrom":sQuery(id+"F2.wireOp",EDGE,"E19")}),-1.0]])]});
            var Q11;
            Q11=makeQuery(id+"F2.imprint","IMPRINT",FACE,{"disambiguationData":[TD([[makeQuery(id+"F2.imprint","IMPRINT",EDGE,{"derivedFrom":sQuery(id+"F2.wireOp",EDGE,"E25")}),-1.0]])]});
            extrude(context, id + "F3", {"entities" : qUnion([Q0, Q1, Q2, Q3, Q4, Q5, Q6, Q7, Q8, Q9, Q10, Q11]), "operationType" : NewBodyOperationType.ADD, "endBound" : BoundingType.SYMMETRIC, "depth" : 2.54 * mm});
        }
    });
